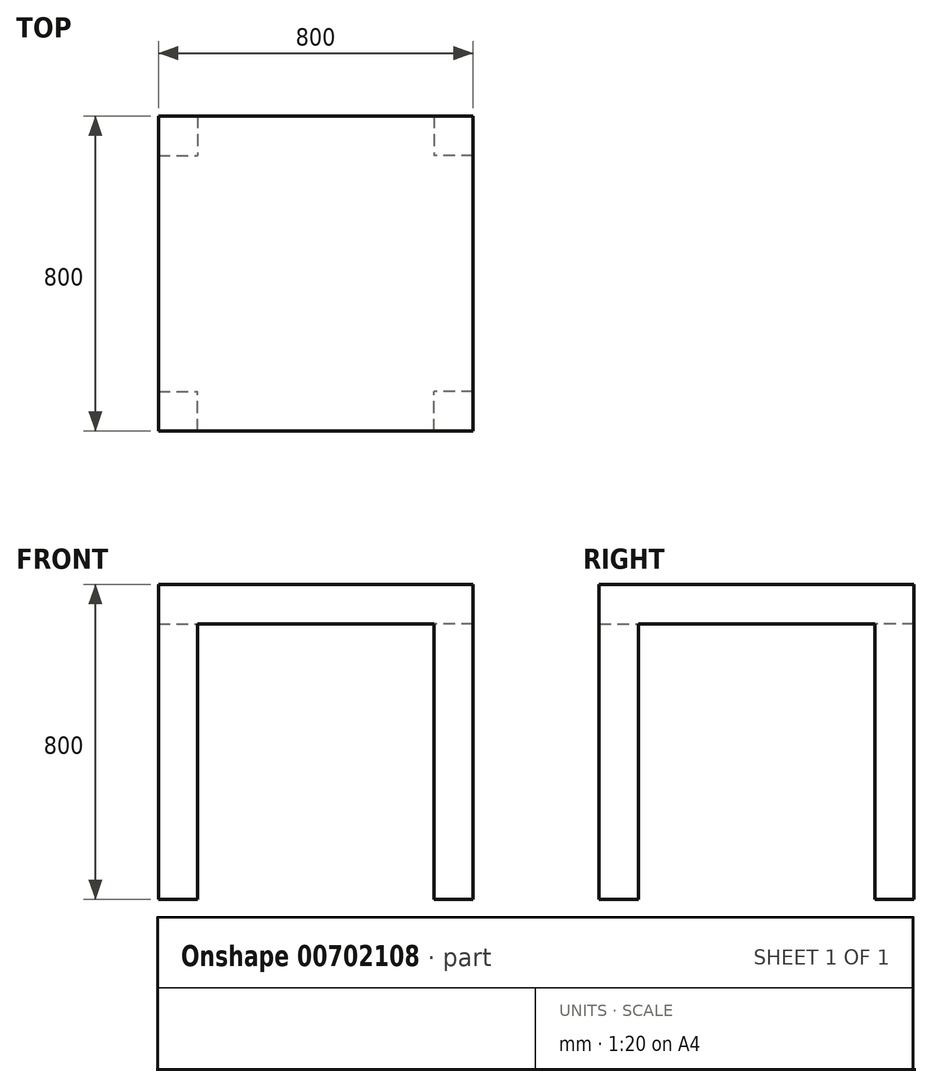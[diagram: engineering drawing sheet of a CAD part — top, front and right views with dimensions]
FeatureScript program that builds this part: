
annotation { "Feature Type Name" : "Feature", "Feature Type Description" : "" }
export const myFeature = defineFeature(function(context is Context, id is Id, definition is map)
    precondition{}
    {
        {
            var Q0;
            Q0=qCreatedBy(makeId("Top.planeOp"),FACE);
            var sketch = newSketch(context, id + "F0", { "sketchPlane" : qUnion([Q0])});
            skLineSegment(sketch, "E0.bottom", {"start": v(0, 0) * mm, "end": v(800, 0) * mm, "construction": true});
            skLineSegment(sketch, "E0.top", {"start": v(0, 800) * mm, "end": v(800, 800) * mm, "construction": true});
            skLineSegment(sketch, "E0.left", {"start": v(0, 0) * mm, "end": v(0, 800) * mm, "construction": true});
            skLineSegment(sketch, "E0.right", {"start": v(800, 0) * mm, "end": v(800, 800) * mm, "construction": true});
            skLineSegment(sketch, "E1.bottom", {"start": v(0, 0) * mm, "end": v(100, 0) * mm});
            skLineSegment(sketch, "E1.top", {"start": v(0, 100) * mm, "end": v(100, 100) * mm});
            skLineSegment(sketch, "E1.left", {"start": v(0, 0) * mm, "end": v(0, 100) * mm});
            skLineSegment(sketch, "E1.right", {"start": v(100, 0) * mm, "end": v(100, 100) * mm});
            skLineSegment(sketch, "E2.bottom", {"start": v(800, 0) * mm, "end": v(700, 0) * mm});
            skLineSegment(sketch, "E2.top", {"start": v(800, 100) * mm, "end": v(700, 100) * mm});
            skLineSegment(sketch, "E2.left", {"start": v(800, 0) * mm, "end": v(800, 100) * mm});
            skLineSegment(sketch, "E2.right", {"start": v(700, 0) * mm, "end": v(700, 100) * mm});
            skLineSegment(sketch, "E3.bottom", {"start": v(0, 800) * mm, "end": v(100, 800) * mm});
            skLineSegment(sketch, "E3.top", {"start": v(0, 700) * mm, "end": v(100, 700) * mm});
            skLineSegment(sketch, "E3.left", {"start": v(0, 800) * mm, "end": v(0, 700) * mm});
            skLineSegment(sketch, "E3.right", {"start": v(100, 800) * mm, "end": v(100, 700) * mm});
            skLineSegment(sketch, "E4.bottom", {"start": v(800, 800) * mm, "end": v(700, 800) * mm});
            skLineSegment(sketch, "E4.top", {"start": v(800, 700) * mm, "end": v(700, 700) * mm});
            skLineSegment(sketch, "E4.left", {"start": v(800, 800) * mm, "end": v(800, 700) * mm});
            skLineSegment(sketch, "E4.right", {"start": v(700, 800) * mm, "end": v(700, 700) * mm});
            skSolve(sketch);
        }
        {
            var Q0;
            Q0=qCreatedBy(makeId("Top.planeOp"),FACE);
            var sketch = newSketch(context, id + "F1", { "sketchPlane" : qUnion([Q0])});
            skLineSegment(sketch, "E5.bottom", {"start": v(0, 0) * mm, "end": v(800, 0) * mm});
            skLineSegment(sketch, "E5.top", {"start": v(0, 800) * mm, "end": v(800, 800) * mm});
            skLineSegment(sketch, "E5.left", {"start": v(0, 0) * mm, "end": v(0, 800) * mm});
            skLineSegment(sketch, "E5.right", {"start": v(800, 0) * mm, "end": v(800, 800) * mm});
            skSolve(sketch);
        }
        {
            var Q0;
            Q0 = qSketchRegion(id + "F1", true);
            extrude(context, id + "F2", {"entities" : qUnion([Q0]), "depth" : 100 * mm, "offsetDistance" : 25 * mm});
        }
        {
            var Q0;
            Q0 = qSketchRegion(id + "F0", true);
            extrude(context, id + "F3", {"entities" : qUnion([Q0]), "operationType" : NewBodyOperationType.ADD, "oppositeDirection" : true, "depth" : 700 * mm, "offsetDistance" : 25 * mm});
        }
    });
